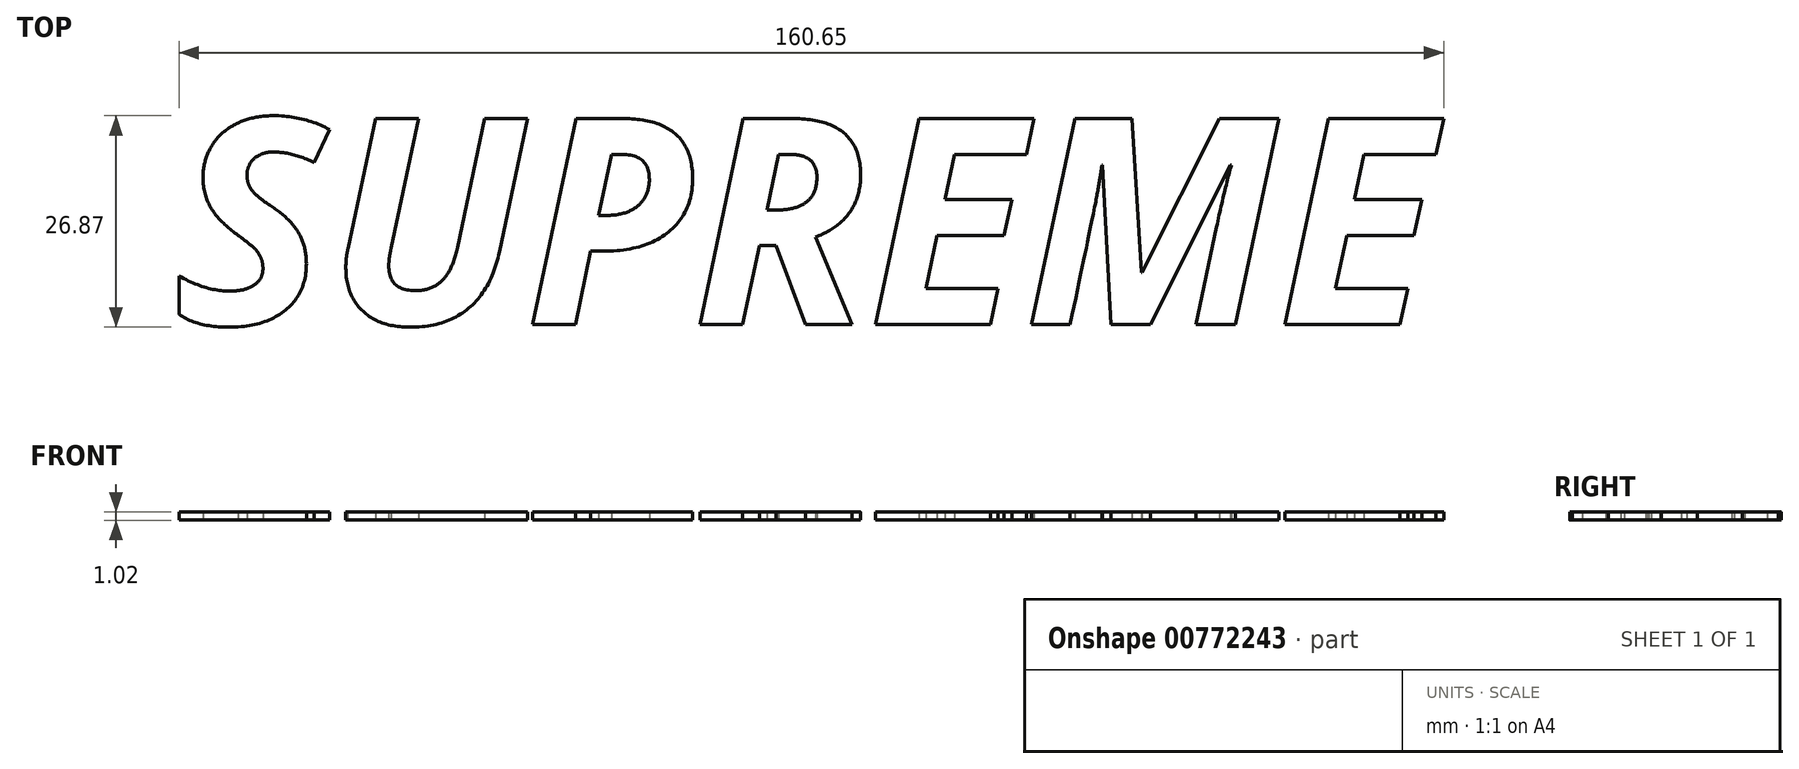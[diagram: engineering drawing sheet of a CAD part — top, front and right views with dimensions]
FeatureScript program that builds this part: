
annotation { "Feature Type Name" : "Feature", "Feature Type Description" : "" }
export const myFeature = defineFeature(function(context is Context, id is Id, definition is map)
    precondition{}
    {
        {
            var Q0;
            Q0=qCreatedBy(makeId("Top.planeOp"),FACE);
            var sketch = newSketch(context, id + "F0", { "sketchPlane" : qUnion([Q0])});
            skText(sketch, "E0", { "text": "SUPREME", "fontName": "OpenSans-BoldItalic.ttf"});
            const initialGuessF0  = {"E0": [-0.08792, 0.02296, 1, 0, 0.02636]};
            skSetInitialGuess(sketch, initialGuessF0);
            skSolve(sketch);
        }
        {
            var Q0;
            Q0 = qConstructionFilter(qBodyType(qCreatedBy(id + "F0" ,EDGE), BodyType.WIRE), ConstructionObject.NO);
            extrude(context, id + "F1", {"bodyType" : ToolBodyType.SURFACE, "surfaceEntities" : qUnion([Q0]), "oppositeDirection" : true, "depth" : 1.02 * mm, "offsetDistance" : 25.4 * mm});
        }
    });
